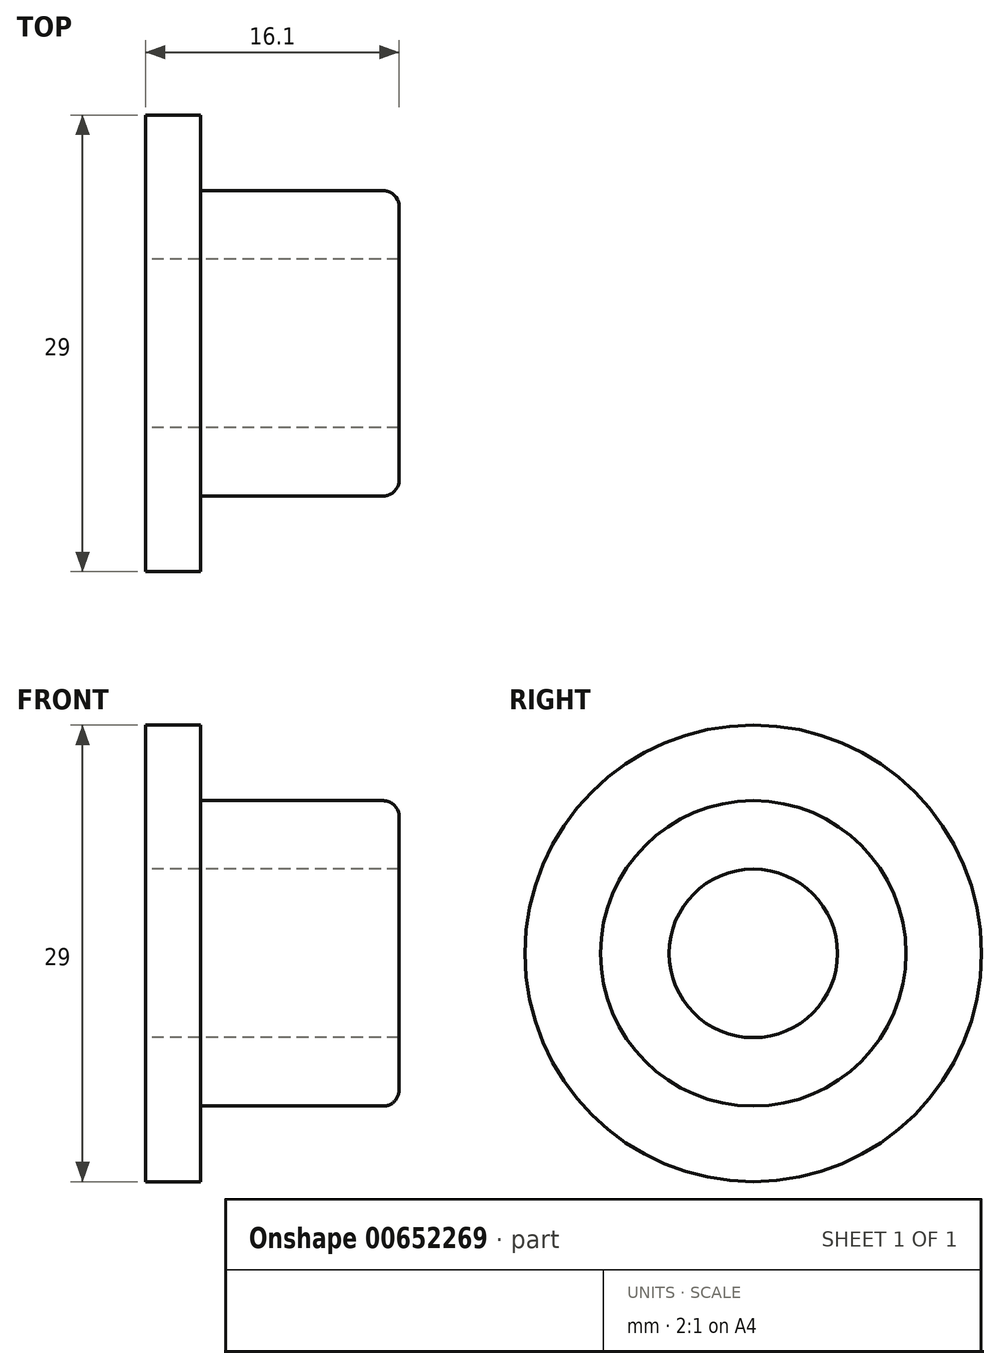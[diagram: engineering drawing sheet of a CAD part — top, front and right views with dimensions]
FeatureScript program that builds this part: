
annotation { "Feature Type Name" : "Feature", "Feature Type Description" : "" }
export const myFeature = defineFeature(function(context is Context, id is Id, definition is map)
    precondition{}
    {
        {
            var Q0;
            Q0=qCreatedBy(makeId("Right.planeOp"),FACE);
            var sketch = newSketch(context, id + "F0", { "sketchPlane" : qUnion([Q0])});
            skCircle(sketch, "E0", {"center": v(0, 0) * mm, "radius": 14.5 * mm});
            skSolve(sketch);
        }
        {
            var Q0;
            Q0 = qSketchRegion(id + "F0", true);
            extrude(context, id + "F1", {"entities" : qUnion([Q0]), "depth" : 3.5 * mm, "offsetDistance" : 25.4 * mm});
        }
        {
            var Q0;
            Q0=qCreatedBy(makeId("Right.planeOp"),FACE);
            var sketch = newSketch(context, id + "F2", { "sketchPlane" : qUnion([Q0])});
            skCircle(sketch, "E1", {"center": v(0, 0) * mm, "radius": 9.7 * mm});
            skSolve(sketch);
        }
        {
            var Q0;
            Q0=makeQuery(id+"F2.imprint","IMPRINT",FACE,{"disambiguationData":[TD([[makeQuery(id+"F2.imprint","IMPRINT",EDGE,{"derivedFrom":sQuery(id+"F2.wireOp",EDGE,"E1")}),1.0]])]});
            var Q1;
            Q1=sQuery(id+"F2.wireOp",EDGE,"E1");
            extrude(context, id + "F3", {"entities" : qUnion([Q0]), "operationType" : NewBodyOperationType.ADD, "surfaceEntities" : qUnion([Q1]), "depth" : 16.1 * mm, "offsetDistance" : 25.4 * mm});
        }
        {
            var Q0;
            Q0=qCreatedBy(makeId("Right.planeOp"),FACE);
            var sketch = newSketch(context, id + "F4", { "sketchPlane" : qUnion([Q0])});
            skCircle(sketch, "E2", {"center": v(0, 0) * mm, "radius": 5.35 * mm});
            skSolve(sketch);
        }
        {
            var Q0;
            Q0=makeQuery(id+"F4.imprint","IMPRINT",FACE,{"disambiguationData":[TD([[makeQuery(id+"F4.imprint","IMPRINT",EDGE,{"derivedFrom":sQuery(id+"F4.wireOp",EDGE,"E2")}),1.0]])]});
            var Q1;
            Q1=sQuery(id+"F4.wireOp",EDGE,"E2");
            extrude(context, id + "F5", {"entities" : qUnion([Q0]), "operationType" : NewBodyOperationType.REMOVE, "surfaceEntities" : qUnion([Q1]), "depth" : 25.4 * mm, "offsetDistance" : 25.4 * mm});
        }
        {
            var Q0;
            Q0=makeQuery(id+"F3.opExtrude","CAP_EDGE",EDGE,{"disambiguationData":[OSD([sQuery(id+"F2.wireOp",EDGE,"E1")])],"isStart":false});
            fillet(context, id + "F6", {"entities" : qUnion([Q0]), "radius" : 1.02 * mm, "tangentPropagation" : true, "allowEdgeOverflow" : false});
        }
    });
